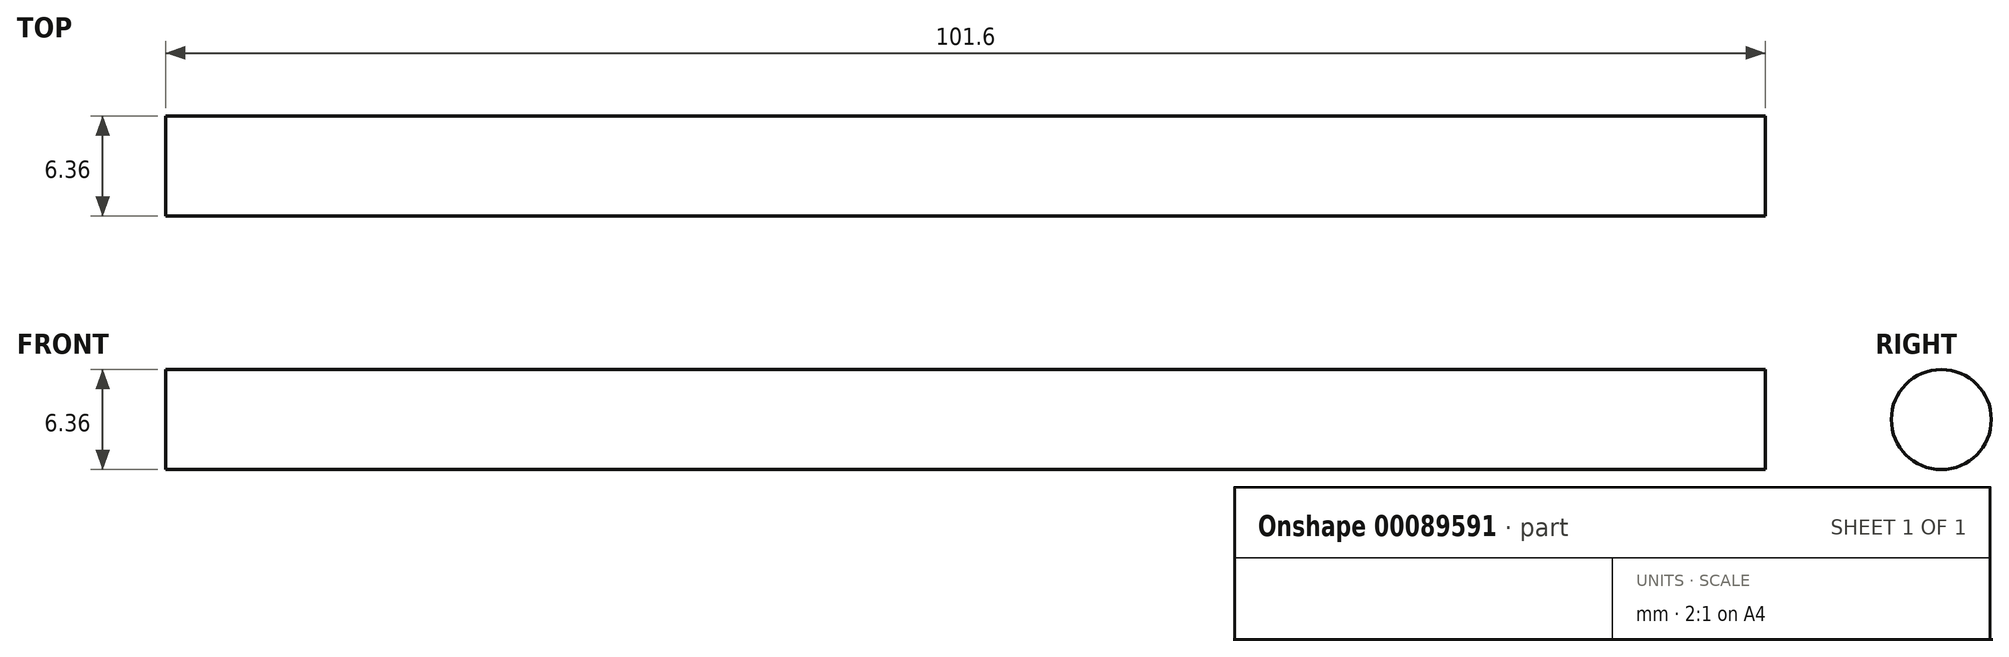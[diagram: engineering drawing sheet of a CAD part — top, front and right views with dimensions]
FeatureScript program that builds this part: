
annotation { "Feature Type Name" : "Feature", "Feature Type Description" : "" }
export const myFeature = defineFeature(function(context is Context, id is Id, definition is map)
    precondition{}
    {
        {
            var Q0;
            Q0=qCreatedBy(makeId("Right.planeOp"),FACE);
            var sketch = newSketch(context, id + "F0", { "sketchPlane" : qUnion([Q0])});
            skCircle(sketch, "E0", {"center": v(0, 0) * mm, "radius": 3.18 * mm});
            skSolve(sketch);
        }
        {
            var Q0;
            Q0=makeQuery(id+"F0.imprint","IMPRINT",FACE,{"disambiguationData":[TD([[makeQuery(id+"F0.imprint","IMPRINT",EDGE,{"derivedFrom":sQuery(id+"F0.wireOp",EDGE,"E0")}),1.0]])]});
            extrude(context, id + "F1", {"entities" : qUnion([Q0]), "depth" : 101.6 * mm});
        }
    });
